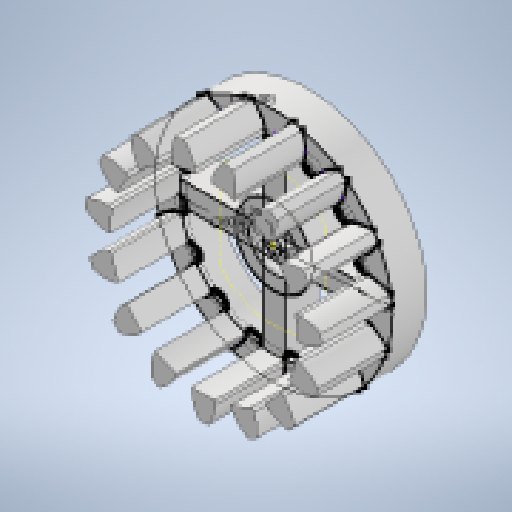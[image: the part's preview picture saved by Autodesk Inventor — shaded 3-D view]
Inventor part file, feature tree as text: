
AUTODESK INVENTOR PART (.ipt)
format: ipt  version: 2023 (Build 270158000, 158)  size: 728,576 bytes
history: native  units: mm
features: extrude x3, other x3, plane x1, reference x1
ambient origin geometry x8: Origin, YZ Plane, XZ Plane, XY Plane, X Axis, Y Axis, Z Axis, Center Point
bodies: Body1 (feature_tree)
feature tree (8):
  extrude  "Extrusion2"  Depth=2.25mm
  extrude  "Extrusion3"  Depth=27.0mm
  plane  "Work Plane1"
  extrude  "Extrusion4"  Depth=0.5mm
  reference  "Reference1"
  parser-record x1  (decoder bookkeeping rows leaked as tree rows — omitted from the tree; the rows remain in map.json)
  other  "Assembly_V7.iam"
  other  "motor:2"
note: 1 file-system path scrubbed to <path> (originals preserved in map.json)
